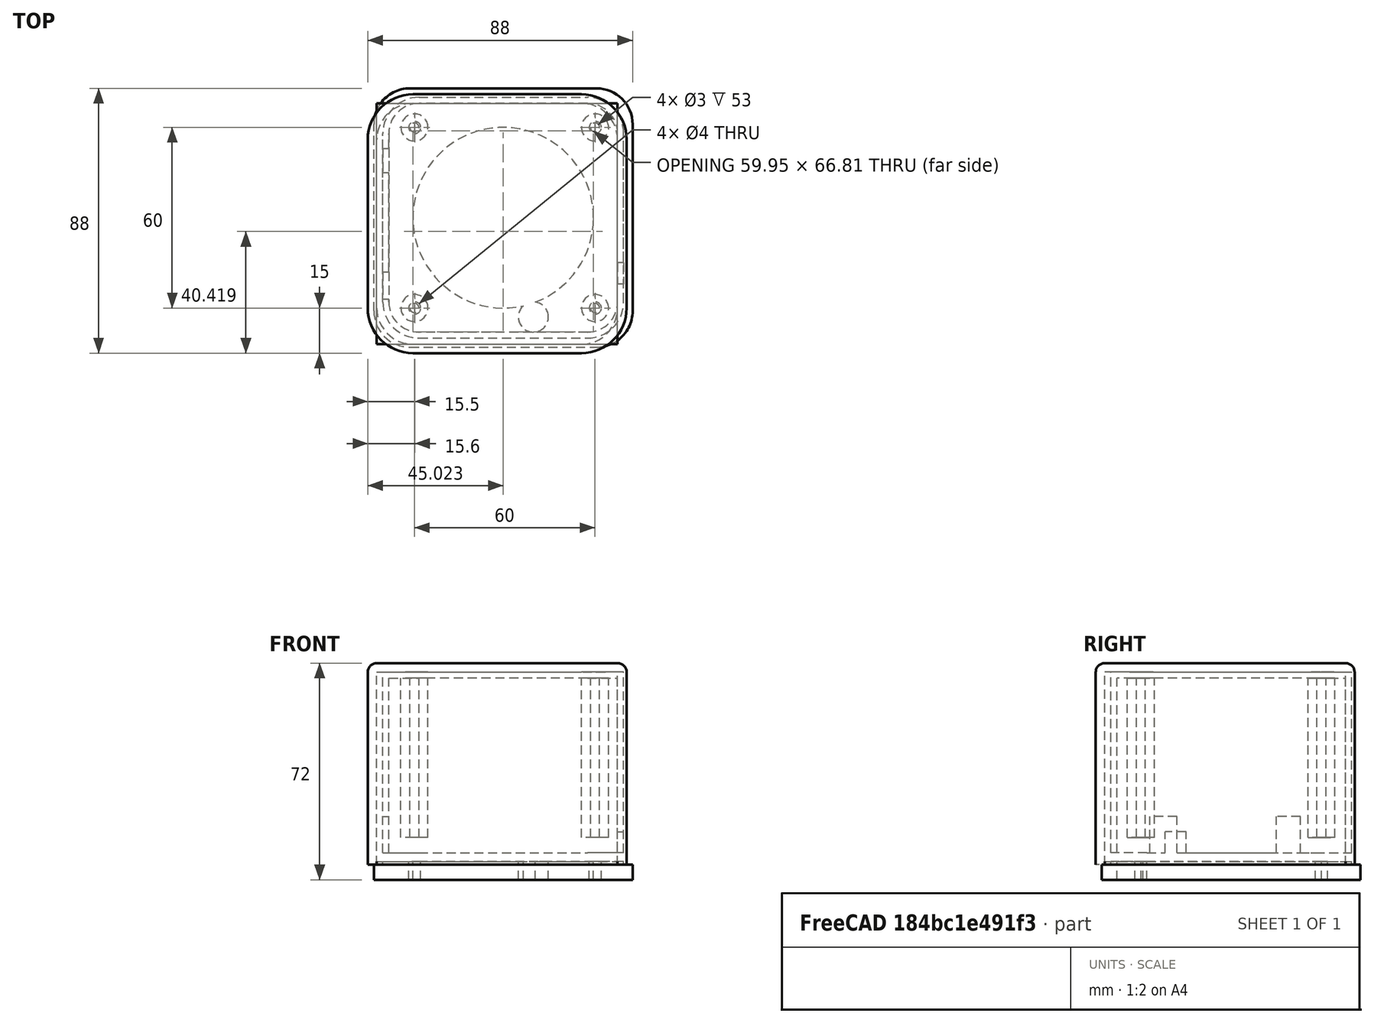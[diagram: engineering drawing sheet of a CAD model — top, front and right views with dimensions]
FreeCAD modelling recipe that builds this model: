
FCSTD DOCUMENT  (FreeCAD 0.17R13522 (Git))
Label: JoselitoBOX_V2
License: All rights reserved
LicenseURL: http://en.wikipedia.org/wiki/All_rights_reserved
objects: Part::Cylinder×12, Part::Box×8, Part::Cut×6, Part::MultiFuse×5, Part::Fillet×4, Part::Thickness×2
note: 37 computed .brp shape members not serialized (recipe doc carries the construction recipe); baked Part::Feature solids carry a one-line shape summary decoded from their .brp

FEATURE [Part::Box] Box002  label="Cubo002"
  AttacherType = Attacher::AttachEngine3D
  Height = 1
  Length = 80
  Width = 80
FEATURE [Part::Box] Box001  label="Cubo001"
  AttacherType = Attacher::AttachEngine3D
  Height = 64
  Length = 80
  Width = 80
FEATURE [Part::Fillet] Fillet
  Base = -> Box001
  Edges = 4 edges r=12: [Edge1,Edge3,Edge5,Edge7]
FEATURE [Part::Thickness] Thickness
  Faces = -> Fillet [Face5]
  Intersection = false
  Join = 0
  Mode = 0
  SelfIntersection = false
  Value = 3
FEATURE [Part::Box] Box  label="Cubo"
  AttacherType = Attacher::AttachEngine3D
  Height = 60
  Length = 80
  Width = 80
FEATURE [Part::Fillet] Fillet001
  Base = -> Box
  Edges = 4 edges r=12: [Edge1,Edge3,Edge5,Edge7]
FEATURE [Part::Thickness] Thickness001  label="CAJA"
  Faces = -> Fillet001 [Face5]
  Intersection = false
  Join = 0
  Mode = 0
  Placement = pos=(2,2,4) rot=(0,0,1;0rad)
  SelfIntersection = false
  Value = -2
FEATURE [Part::Cut] Cut001
  Placement = pos=(5.5,5,6) rot=(0,0,1;0rad)
FEATURE [Part::Cylinder] Cylinder002  label="Cilindro002"
  Angle = 360
  AttacherType = Attacher::AttachEngine3D
  Height = 63
  Placement = pos=(7,7,3) rot=(0,0,1;0rad)
  Radius = 1.5
FEATURE [Part::Cylinder] Cylinder003  label="Cilindro003"
  Angle = 360
  AttacherType = Attacher::AttachEngine3D
  Height = 55
  Placement = pos=(7,7,3) rot=(0,0,1;0rad)
  Radius = 4.5
FEATURE [Part::Cut] Cut002
  Base = -> Cylinder003
  Placement = pos=(5.5,65,6) rot=(0,0,1;0rad)
  Tool = -> Cylinder002
FEATURE [Part::Cylinder] Cylinder004  label="Cilindro004"
  Angle = 360
  AttacherType = Attacher::AttachEngine3D
  Height = 63
  Placement = pos=(7,7,3) rot=(0,0,1;0rad)
  Radius = 1.5
FEATURE [Part::Cylinder] Cylinder005  label="Cilindro005"
  Angle = 360
  AttacherType = Attacher::AttachEngine3D
  Height = 55
  Placement = pos=(7,7,3) rot=(0,0,1;0rad)
  Radius = 4.5
FEATURE [Part::Cut] Cut003
  Base = -> Cylinder005
  Placement = pos=(65.5,65,6) rot=(0,0,1;0rad)
  Tool = -> Cylinder004
FEATURE [Part::Cylinder] Cylinder006  label="Cilindro006"
  Angle = 360
  AttacherType = Attacher::AttachEngine3D
  Height = 63
  Placement = pos=(7,7,3) rot=(0,0,1;0rad)
  Radius = 1.5
FEATURE [Part::Cylinder] Cylinder007  label="Cilindro007"
  Angle = 360
  AttacherType = Attacher::AttachEngine3D
  Height = 55
  Placement = pos=(7,7,3) rot=(0,0,1;0rad)
  Radius = 4.5
FEATURE [Part::Cut] Cut004
  Base = -> Cylinder007
  Placement = pos=(65.5,5,6) rot=(0,0,1;0rad)
  Tool = -> Cylinder006
FEATURE [Part::MultiFuse] Fusion  label="cilindros"
  Shapes = -> [Cut001,Cut003,Cut004,Cut002]
FEATURE [Part::Box] Box003  label="Cubo003"
  AttacherType = Attacher::AttachEngine3D
  Height = 1
  Length = 80
  Width = 80
FEATURE [Part::Fillet] Fillet002
  Base = -> Box003
  Edges = 4 edges r=12: [Edge1,Edge3,Edge5,Edge7]
FEATURE [Part::Box] Box004  label="Cubo004"
  AttacherType = Attacher::AttachEngine3D
  Height = 5
  Length = 86
  Width = 86
FEATURE [Part::Fillet] Fillet003
  Base = -> Box004
  Edges = 4 edges r=12: [Edge1,Edge3,Edge5,Edge7]
  Placement = pos=(-3,-3,-5) rot=(0,0,1;0rad)
FEATURE [Part::Cylinder] Cylinder008  label="Speaker"
  Angle = 360
  AttacherType = Attacher::AttachEngine3D
  Height = 10
  Placement = pos=(42,42,-6) rot=(0,0,1;0rad)
  Radius = 30
FEATURE [Part::Cylinder] Cylinder009  label="LED"
  Angle = 360
  AttacherType = Attacher::AttachEngine3D
  Height = 10
  Placement = pos=(52,9,-6) rot=(0,0,1;0rad)
  Radius = 5
FEATURE [Part::MultiFuse] Fusion001  label="Tapa"
  Placement = pos=(2,2,0) rot=(0,0,1;0rad)
  Shapes = -> [Fillet002,Fillet003]
FEATURE [Part::Cylinder] Cylinder011  label="rod1"
  Angle = 360
  AttacherType = Attacher::AttachEngine3D
  Height = 63
  Placement = pos=(72.6,12,-9) rot=(0,0,1;0rad)
  Radius = 2
FEATURE [Part::Cylinder] Cylinder012  label="rod2"
  Angle = 360
  AttacherType = Attacher::AttachEngine3D
  Height = 63
  Placement = pos=(72.6,72,-9) rot=(0,0,1;0rad)
  Radius = 2
FEATURE [Part::Cylinder] Cylinder013  label="rod3"
  Angle = 360
  AttacherType = Attacher::AttachEngine3D
  Height = 63
  Placement = pos=(12.6,12,-9) rot=(0,0,1;0rad)
  Radius = 2
FEATURE [Part::Cylinder] Cylinder014  label="rod4"
  Angle = 360
  AttacherType = Attacher::AttachEngine3D
  Height = 63
  Placement = pos=(12.6,72,-9) rot=(0,0,1;0rad)
  Radius = 2
FEATURE [Part::Box] Box009  label="interruptor002"
  AttacherType = Attacher::AttachEngine3D
  Height = 17
  Length = 26
  Placement = pos=(62,20,-6) rot=(0,0,1;0rad)
  Width = 7
FEATURE [Part::Box] Box010  label="jackDC"
  AttacherType = Attacher::AttachEngine3D
  Height = 12
  Length = 26
  Placement = pos=(-4,15,4) rot=(0,0,1;0rad)
  Width = 9
FEATURE [Part::Box] Box011  label="jackAudio"
  AttacherType = Attacher::AttachEngine3D
  Height = 12
  Length = 26
  Placement = pos=(-4,57,4) rot=(0,0,1;0rad)
  Width = 8
FEATURE [Part::MultiFuse] Fusion002
  Shapes = -> [Box009,Box010,Box011]
FEATURE [Part::Cut] Cut  label="BOX"
  Base = -> Thickness001
  Tool = -> Fusion002
FEATURE [Part::MultiFuse] Fusion003  label="holes"
  Shapes = -> [Cylinder011,Cylinder009,Cylinder008,Cylinder012,Cylinder013,Cylinder014]
FEATURE [Part::Cut] Cut005  label="frontspeaker"
  Base = -> Fusion001
  Tool = -> Fusion003
FEATURE [Part::MultiFuse] Fusion004  label="BOX001"
  Shapes = -> [Fusion,Cut]
